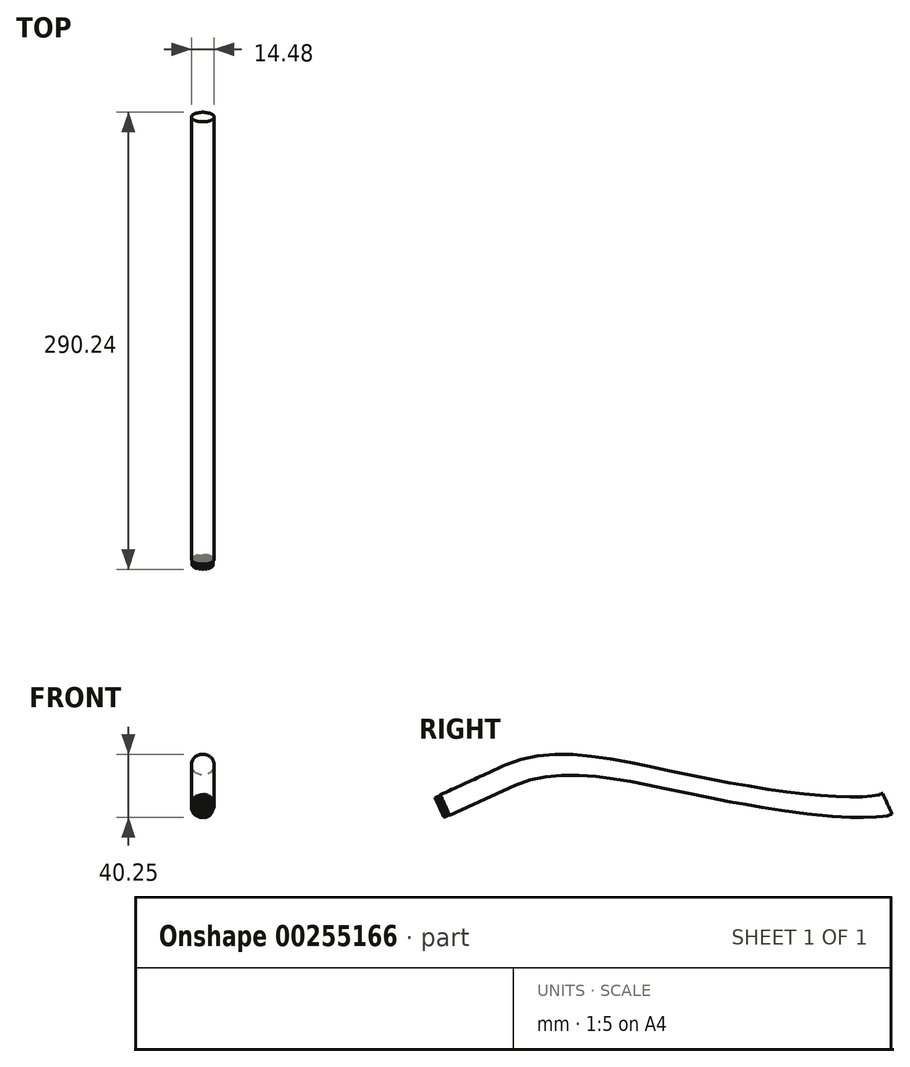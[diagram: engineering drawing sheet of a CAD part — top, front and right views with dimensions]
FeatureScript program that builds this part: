
annotation { "Feature Type Name" : "Feature", "Feature Type Description" : "" }
export const myFeature = defineFeature(function(context is Context, id is Id, definition is map)
    precondition{}
    {
        {
            var Q0;
            Q0=qCreatedBy(makeId("Right.planeOp"),FACE);
            var sketch = newSketch(context, id + "F0", { "sketchPlane" : qUnion([Q0])});
            skFitSpline(sketch, "E0", {"points": [v(0, 0) * mm, v(107.4, -4.5) * mm, v(215, -20.32) * mm, v(239.38, -18) * mm], "startDerivative": vector(220.1, 100.8) * mm, "endDerivative": vector(20.71, 23.57) * mm});
            skSolve(sketch);
        }
        {
            var Q0;
            Q0=sQuery(id+"F0.wireOp",EDGE,"E0");
            var Q1;
            Q1=sQuery(id+"F0.wireOp",VERTEX,"E0.start");
            cPlane(context, id + "F1", {"entities" : qUnion([Q0, Q1]), "cplaneType" : CPlaneType.CURVE_POINT, "offset" : 25.4 * mm, "width" : 152.4 * mm, "height" : 152.4 * mm});
        }
        {
            var Q0;
            Q0=qCreatedBy(id+"F1.planeOp",FACE);
            var sketch = newSketch(context, id + "F2", { "sketchPlane" : qUnion([Q0])});
            skCircle(sketch, "E1", {"center": v(0, 0) * mm, "radius": 7.24 * mm});
            skSolve(sketch);
        }
        {
            var Q0;
            Q0=makeQuery(id+"F2.imprint","IMPRINT",FACE,{"disambiguationData":[TD([[makeQuery(id+"F2.imprint","IMPRINT",EDGE,{"derivedFrom":sQuery(id+"F2.wireOp",EDGE,"E1")}),1.0]])]});
            var Q1;
            Q1=sQuery(id+"F0.wireOp",EDGE,"E0");
            sweep(context, id + "F3", {"profiles" : qUnion([Q0]), "path" : qUnion([Q1]), "keepProfileOrientation" : true});
        }
        {
            var Q0;
            Q0=qCreatedBy(makeId("Right.planeOp"),FACE);
            var sketch = newSketch(context, id + "F4", { "sketchPlane" : qUnion([Q0])});
            skLineSegment(sketch, "E2", {"start": v(0, 0) * mm, "end": v(-41.57, -19.04) * mm});
            skSolve(sketch);
        }
        {
            var Q0;
            Q0=makeQuery(id+"F2.imprint","IMPRINT",FACE,{"disambiguationData":[TD([[makeQuery(id+"F2.imprint","IMPRINT",EDGE,{"derivedFrom":sQuery(id+"F2.wireOp",EDGE,"E1")}),1.0]])]});
            var Q1;
            Q1=sQuery(id+"F4.wireOp",EDGE,"E2");
            sweep(context, id + "F5", {"operationType" : NewBodyOperationType.ADD, "profiles" : qUnion([Q0]), "path" : qUnion([Q1])});
        }
        {
            var Q0;
            Q0=makeQuery(id+"F5.opSweep","CAP_FACE",FACE,{"disambiguationData":[OSD([sQuery(id+"F2.wireOp",EDGE,"E1"),sQuery(id+"F4.wireOp",VERTEX,"E2.end")])],"isStart":false});
            var sketch = newSketch(context, id + "F6", { "sketchPlane" : qUnion([Q0])});
            skCircle(sketch, "E3", {"center": v(0, 6.13) * mm, "radius": 0.64 * mm});
            skLineSegment(sketch, "E4", {"start": v(0, 7.24) * mm, "end": v(0, -7.24) * mm, "construction": true});
            skCircle(sketch, "E5.1.0", {"center": v(-2.1, 5.76) * mm, "radius": 0.64 * mm});
            skCircle(sketch, "E5.2.0", {"center": v(-3.94, 4.7) * mm, "radius": 0.64 * mm});
            skCircle(sketch, "E5.3.0", {"center": v(-5.3, 3.06) * mm, "radius": 0.64 * mm});
            skCircle(sketch, "E5.4.0", {"center": v(-6.03, 1.06) * mm, "radius": 0.64 * mm});
            skCircle(sketch, "E5.5.0", {"center": v(-6.03, -1.06) * mm, "radius": 0.64 * mm});
            skCircle(sketch, "E5.6.0", {"center": v(-5.3, -3.06) * mm, "radius": 0.64 * mm});
            skCircle(sketch, "E5.7.0", {"center": v(-3.94, -4.7) * mm, "radius": 0.64 * mm});
            skCircle(sketch, "E5.8.0", {"center": v(-2.1, -5.76) * mm, "radius": 0.64 * mm});
            skCircle(sketch, "E5.9.0", {"center": v(0, -6.13) * mm, "radius": 0.64 * mm});
            skCircle(sketch, "E5.10.0", {"center": v(2.1, -5.76) * mm, "radius": 0.64 * mm});
            skCircle(sketch, "E5.11.0", {"center": v(3.94, -4.7) * mm, "radius": 0.64 * mm});
            skCircle(sketch, "E5.12.0", {"center": v(5.3, -3.06) * mm, "radius": 0.64 * mm});
            skCircle(sketch, "E5.13.0", {"center": v(6.03, -1.06) * mm, "radius": 0.64 * mm});
            skCircle(sketch, "E5.14.0", {"center": v(6.03, 1.06) * mm, "radius": 0.64 * mm});
            skCircle(sketch, "E5.15.0", {"center": v(5.3, 3.06) * mm, "radius": 0.64 * mm});
            skCircle(sketch, "E5.16.0", {"center": v(3.94, 4.7) * mm, "radius": 0.64 * mm});
            skCircle(sketch, "E5.17.0", {"center": v(2.1, 5.76) * mm, "radius": 0.64 * mm});
            skPoint(sketch, "E5.center", {"position": v(0, 0) * mm});
            skCircle(sketch, "E6", {"center": v(0.02, 3.8) * mm, "radius": 0.64 * mm});
            skCircle(sketch, "E7.1.0", {"center": v(-2.67, 2.7) * mm, "radius": 0.64 * mm});
            skCircle(sketch, "E7.2.0", {"center": v(-3.8, 0.02) * mm, "radius": 0.64 * mm});
            skCircle(sketch, "E7.3.0", {"center": v(-2.7, -2.67) * mm, "radius": 0.64 * mm});
            skCircle(sketch, "E7.4.0", {"center": v(-0.02, -3.8) * mm, "radius": 0.64 * mm});
            skCircle(sketch, "E7.5.0", {"center": v(2.67, -2.7) * mm, "radius": 0.64 * mm});
            skCircle(sketch, "E7.6.0", {"center": v(3.8, -0.02) * mm, "radius": 0.64 * mm});
            skCircle(sketch, "E7.7.0", {"center": v(2.7, 2.67) * mm, "radius": 0.64 * mm});
            skCircle(sketch, "E8", {"center": v(0.01, 1.72) * mm, "radius": 0.64 * mm});
            skCircle(sketch, "E9.1.0", {"center": v(-1.48, 0.87) * mm, "radius": 0.64 * mm});
            skCircle(sketch, "E9.2.0", {"center": v(-1.5, -0.85) * mm, "radius": 0.64 * mm});
            skCircle(sketch, "E9.3.0", {"center": v(-0.01, -1.72) * mm, "radius": 0.64 * mm});
            skCircle(sketch, "E9.4.0", {"center": v(1.48, -0.87) * mm, "radius": 0.64 * mm});
            skCircle(sketch, "E9.5.0", {"center": v(1.5, 0.85) * mm, "radius": 0.64 * mm});
            skSolve(sketch);
        }
        {
            var Q0;
            Q0 = qSketchRegion(id + "F6", true);
            extrude(context, id + "F7", {"entities" : qUnion([Q0]), "depth" : 3.8 * mm, "offsetDistance" : 25.4 * mm});
        }
    });
